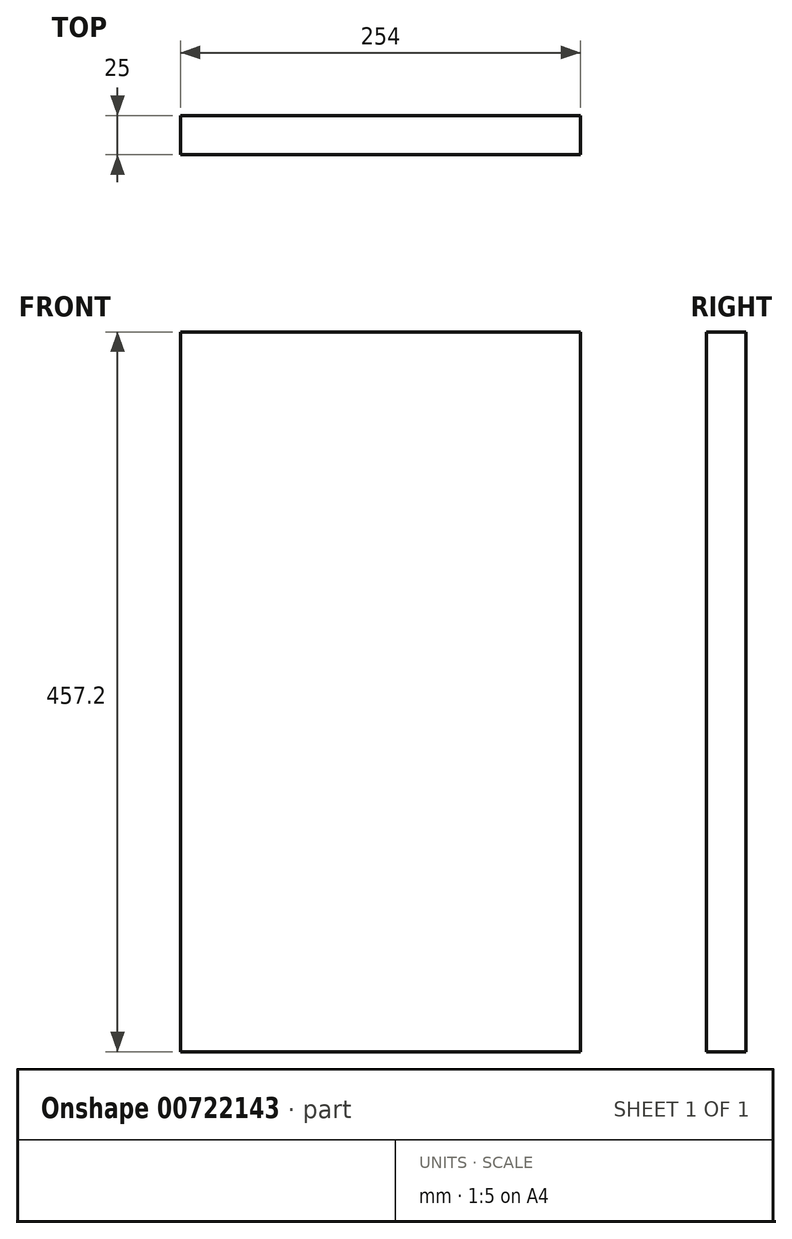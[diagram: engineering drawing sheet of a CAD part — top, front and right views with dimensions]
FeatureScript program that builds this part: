
annotation { "Feature Type Name" : "Feature", "Feature Type Description" : "" }
export const myFeature = defineFeature(function(context is Context, id is Id, definition is map)
    precondition{}
    {
        {
            var Q0;
            Q0=qCreatedBy(makeId("Front.planeOp"),FACE);
            var sketch = newSketch(context, id + "F0", { "sketchPlane" : qUnion([Q0])});
            skPoint(sketch, "E0.middle", {"position": v(0, 0) * mm});
            skLineSegment(sketch, "E1.bottom", {"start": v(127, -228.6) * mm, "end": v(-127, -228.6) * mm});
            skLineSegment(sketch, "E1.top", {"start": v(127, 228.6) * mm, "end": v(-127, 228.6) * mm});
            skLineSegment(sketch, "E1.left", {"start": v(127, -228.6) * mm, "end": v(127, 228.6) * mm});
            skLineSegment(sketch, "E1.right", {"start": v(-127, -228.6) * mm, "end": v(-127, 228.6) * mm});
            skSolve(sketch);
        }
        {
            var Q0;
            Q0=makeQuery(id+"F0.imprint","IMPRINT",FACE,{"disambiguationData":[TD([[makeQuery(id+"F0.imprint","IMPRINT",EDGE,{"derivedFrom":sQuery(id+"F0.wireOp",EDGE,"E1.bottom")}),-1.0]])]});
            extrude(context, id + "F1", {"entities" : qUnion([Q0]), "depth" : 25 * mm, "offsetDistance" : 25 * mm});
        }
    });
